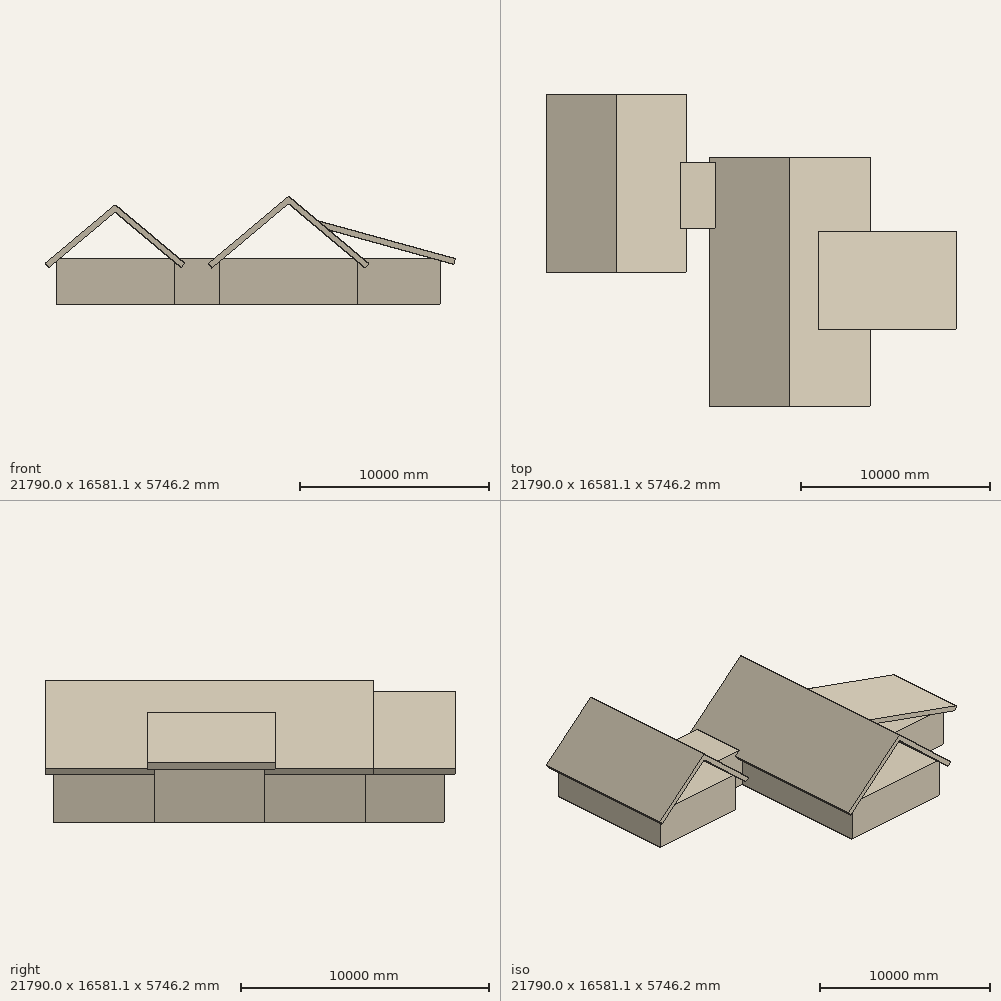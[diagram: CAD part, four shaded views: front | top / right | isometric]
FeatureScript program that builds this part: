
annotation { "Feature Type Name" : "Feature", "Feature Type Description" : "" }
export const myFeature = defineFeature(function(context is Context, id is Id, definition is map)
    precondition{}
    {
        {
            var Q0;
            Q0=qCreatedBy(makeId("Top.planeOp"),FACE);
            var sketch = newSketch(context, id + "F0", { "sketchPlane" : qUnion([Q0])});
            skLineSegment(sketch, "E0", {"start": v(0, 0) * mm, "end": v(7315.2, 0) * mm});
            skLineSegment(sketch, "E1", {"start": v(7315.2, 0) * mm, "end": v(7315.2, -9296.4) * mm});
            skLineSegment(sketch, "E2", {"start": v(7315.2, -9296.4) * mm, "end": v(0, -9296.4) * mm});
            skLineSegment(sketch, "E3", {"start": v(0, -9296.4) * mm, "end": v(0, 0) * mm});
            skLineSegment(sketch, "E4", {"start": v(7315.2, -4114.8) * mm, "end": v(11734.8, -4114.8) * mm});
            skLineSegment(sketch, "E5", {"start": v(11734.8, -4114.8) * mm, "end": v(11734.8, -8534.4) * mm});
            skLineSegment(sketch, "E6", {"start": v(11734.8, -8534.4) * mm, "end": v(7315.2, -8534.4) * mm});
            skLineSegment(sketch, "E7", {"start": v(7315.2, -9296.4) * mm, "end": v(7315.2, -12649.2) * mm});
            skLineSegment(sketch, "E8", {"start": v(7315.2, -12649.2) * mm, "end": v(0, -12649.2) * mm});
            skLineSegment(sketch, "E9", {"start": v(0, -12649.2) * mm, "end": v(0, -9296.4) * mm});
            skLineSegment(sketch, "E10", {"start": v(0, 0) * mm, "end": v(-2438.4, 0) * mm});
            skLineSegment(sketch, "E11", {"start": v(-2438.4, 3200.4) * mm, "end": v(-2438.4, -5334) * mm});
            skLineSegment(sketch, "E12", {"start": v(-2438.4, -3505.2) * mm, "end": v(0, -3505.2) * mm});
            skLineSegment(sketch, "E13", {"start": v(-2438.4, -5334) * mm, "end": v(-8686.8, -5334) * mm});
            skLineSegment(sketch, "E14", {"start": v(-8686.8, -5334) * mm, "end": v(-8686.8, 3200.4) * mm});
            skLineSegment(sketch, "E15", {"start": v(-8686.8, 3200.4) * mm, "end": v(-2438.4, 3200.4) * mm});
            skSolve(sketch);
        }
        {
            var Q0;
            {var subQ4=sQuery(id+"F0.wireOp",EDGE,"E0");Q0=makeQuery(id+"F0.imprint","IMPRINT",FACE,{"disambiguationData":[TD([[makeQuery(id+"F0.imprint","IMPRINT",EDGE,{"derivedFrom":subQ4}),-1.0]])]});}
            var Q1;
            Q1=makeQuery(id+"F0.imprint","IMPRINT",FACE,{"disambiguationData":[TD([[makeQuery(id+"F0.imprint","IMPRINT",EDGE,{"derivedFrom":sQuery(id+"F0.wireOp",EDGE,"E2")}),1.0]])]});
            var Q2;
            {var subQ0=sQuery(id+"F0.wireOp",EDGE,"E10");Q2=makeQuery(id+"F0.imprint","IMPRINT",FACE,{"disambiguationData":[TD([[makeQuery(id+"F0.imprint","IMPRINT",EDGE,{"derivedFrom":subQ0}),1.0]])]});}
            var Q3;
            {var subQ0=sQuery(id+"F0.wireOp",EDGE,"E4");Q3=makeQuery(id+"F0.imprint","IMPRINT",FACE,{"disambiguationData":[TD([[makeQuery(id+"F0.imprint","IMPRINT",EDGE,{"derivedFrom":subQ0}),-1.0]])]});}
            var Q4;
            {var subQ0=sQuery(id+"F0.wireOp",EDGE,"E13");Q4=makeQuery(id+"F0.imprint","IMPRINT",FACE,{"disambiguationData":[TD([[makeQuery(id+"F0.imprint","IMPRINT",EDGE,{"derivedFrom":subQ0}),-1.0]])]});}
            extrude(context, id + "F1", {"entities" : qUnion([Q0, Q1, Q2, Q3, Q4]), "depth" : 2438.4 * mm});
        }
        {
            var Q0;
            Q0=makeQuery(id+"F1.opExtrude","SWEPT_FACE",FACE,{"disambiguationData":[OSD([sQuery(id+"F0.wireOp",EDGE,"E8")])]});
            var sketch = newSketch(context, id + "F2", { "sketchPlane" : qUnion([Q0])});
            skLineSegment(sketch, "E16", {"start": v(3657.6, 4572) * mm, "end": v(3657.6, 5746.22) * mm});
            skPoint(sketch, "E16.endSnap0", {"position": v(3657.6, 2438.4) * mm});
            skLineSegment(sketch, "E17", {"start": v(3657.6, 5746.22) * mm, "end": v(-609.6, 2165.62) * mm});
            skLineSegment(sketch, "E18", {"start": v(-609.6, 2165.62) * mm, "end": v(-413.68, 1932.13) * mm});
            skLineSegment(sketch, "E19", {"start": v(-413.68, 1932.13) * mm, "end": v(3657.6, 5348.34) * mm});
            skLineSegment(sketch, "E20.MirrorCS", {"start": v(7924.8, 2165.62) * mm, "end": v(7728.88, 1932.13) * mm});
            skLineSegment(sketch, "E21.MirrorCS", {"start": v(3657.6, 5746.22) * mm, "end": v(7924.8, 2165.62) * mm});
            skLineSegment(sketch, "E22.MirrorCS", {"start": v(7728.88, 1932.13) * mm, "end": v(3657.6, 5348.34) * mm});
            skPoint(sketch, "E23.orphan", {"position": v(189.67, 2438.4) * mm});
            skPoint(sketch, "E24.orphan", {"position": v(7125.53, 2438.4) * mm});
            skSolve(sketch);
        }
        {
            var Q0;
            Q0=makeQuery(id+"F2.imprint","IMPRINT",FACE,{"disambiguationData":[TD([[makeQuery(id+"F2.imprint","IMPRINT",EDGE,{"derivedFrom":sQuery(id+"F2.wireOp",EDGE,"E16")}),1.0]])]});
            var Q1;
            Q1=makeQuery(id+"F2.imprint","IMPRINT",FACE,{"disambiguationData":[TD([[makeQuery(id+"F2.imprint","IMPRINT",EDGE,{"derivedFrom":sQuery(id+"F2.wireOp",EDGE,"E16")}),-1.0]])]});
            var Q2;
            {var subQ0=sQuery(id+"F2.wireOp",EDGE,"E19");var subQ1=sQuery(id+"F0.wireOp",EDGE,"E8");var subQ4=makeQuery(id+"F1.opExtrude","CAP_EDGE",EDGE,{"disambiguationData":[OSD([subQ1])],"isStart":false});var subQ5=makeQuery(id+"F2.imprint","INTERSECT",VERTEX,{"derivedFrom":[subQ4,subQ0]});Q2=makeQuery(id+"F2.imprint","IMPRINT",FACE,{"disambiguationData":[TD([[makeQuery(id+"F2.imprint","IMPRINT",EDGE,{"disambiguationData":[TD([[subQ5,1.0]])],"derivedFrom":subQ0}),1.0]])]});}
            var Q3;
            {var subQ0=sQuery(id+"F2.wireOp",EDGE,"E22.MirrorCS");var subQ1=sQuery(id+"F0.wireOp",EDGE,"E8");var subQ4=makeQuery(id+"F1.opExtrude","CAP_EDGE",EDGE,{"disambiguationData":[OSD([subQ1])],"isStart":false});var subQ5=makeQuery(id+"F2.imprint","INTERSECT",VERTEX,{"derivedFrom":[subQ4,subQ0]});Q3=makeQuery(id+"F2.imprint","IMPRINT",FACE,{"disambiguationData":[TD([[makeQuery(id+"F2.imprint","IMPRINT",EDGE,{"disambiguationData":[TD([[subQ5,1.0]])],"derivedFrom":subQ0}),-1.0]])]});}
            var Q4;
            Q4=makeQuery(id+"F1.opExtrude","SWEPT_FACE",FACE,{"disambiguationData":[OSD([sQuery(id+"F0.wireOp",EDGE,"E0"),sQuery(id+"F0.wireOp",EDGE,"E10")])]});
            extrude(context, id + "F3", {"entities" : qUnion([Q0, Q1, Q2, Q3]), "operationType" : NewBodyOperationType.ADD, "endBoundEntityFace" : qUnion([Q4]), "depth" : 304.8 * mm, "hasSecondDirection" : true, "secondDirectionOppositeDirection" : true, "secondDirectionDepth" : 12954 * mm});
        }
        {
            var Q0;
            Q0=makeQuery(id+"F1.opExtrude","SWEPT_FACE",FACE,{"disambiguationData":[OSD([sQuery(id+"F0.wireOp",EDGE,"E6")])]});
            var sketch = newSketch(context, id + "F4", { "sketchPlane" : qUnion([Q0])});
            skLineSegment(sketch, "E25", {"start": v(5772.08, 3971.96) * mm, "end": v(12435.47, 2136.43) * mm});
            skLineSegment(sketch, "E26", {"start": v(12435.47, 2136.43) * mm, "end": v(12518.66, 2438.4) * mm});
            skLineSegment(sketch, "E27", {"start": v(12518.66, 2438.4) * mm, "end": v(5195.68, 4455.62) * mm});
            skLineSegment(sketch, "E28", {"start": v(5195.68, 4455.62) * mm, "end": v(5772.08, 3971.96) * mm});
            skSolve(sketch);
        }
        {
            var Q0;
            Q0 = qSketchRegion(id + "F4", true);
            extrude(context, id + "F5", {"entities" : qUnion([Q0]), "operationType" : NewBodyOperationType.ADD, "depth" : 304.8 * mm, "hasSecondDirection" : true, "secondDirectionOppositeDirection" : true, "secondDirectionDepth" : 4876.8 * mm});
        }
        {
            var Q0;
            Q0=makeQuery(id+"F1.opExtrude","SWEPT_FACE",FACE,{"disambiguationData":[OSD([sQuery(id+"F0.wireOp",EDGE,"E13")])]});
            var sketch = newSketch(context, id + "F6", { "sketchPlane" : qUnion([Q0])});
            skLineSegment(sketch, "E29", {"start": v(-5562.6, 4900.76) * mm, "end": v(-5562.6, 5298.65) * mm});
            skPoint(sketch, "E29.endSnap0", {"position": v(-5562.6, 2438.4) * mm});
            skLineSegment(sketch, "E30", {"start": v(-5562.6, 5298.65) * mm, "end": v(-9271.33, 2186.65) * mm});
            skLineSegment(sketch, "E31", {"start": v(-9271.33, 2186.65) * mm, "end": v(-9075.41, 1953.16) * mm});
            skLineSegment(sketch, "E32", {"start": v(-9075.41, 1953.16) * mm, "end": v(-5562.6, 4900.76) * mm});
            skLineSegment(sketch, "E33.MirrorCS", {"start": v(-1853.87, 2186.65) * mm, "end": v(-2049.79, 1953.16) * mm});
            skLineSegment(sketch, "E34.MirrorCS", {"start": v(-2049.79, 1953.16) * mm, "end": v(-5562.6, 4900.76) * mm});
            skLineSegment(sketch, "E35.MirrorCS", {"start": v(-5562.6, 5298.65) * mm, "end": v(-1853.87, 2186.65) * mm});
            skSolve(sketch);
        }
        {
            var Q0;
            Q0 = qSketchRegion(id + "F6", true);
            extrude(context, id + "F7", {"entities" : qUnion([Q0]), "operationType" : NewBodyOperationType.ADD, "depth" : 518.16 * mm, "hasSecondDirection" : true, "secondDirectionOppositeDirection" : true, "secondDirectionDepth" : 8961.12 * mm});
        }
    });
